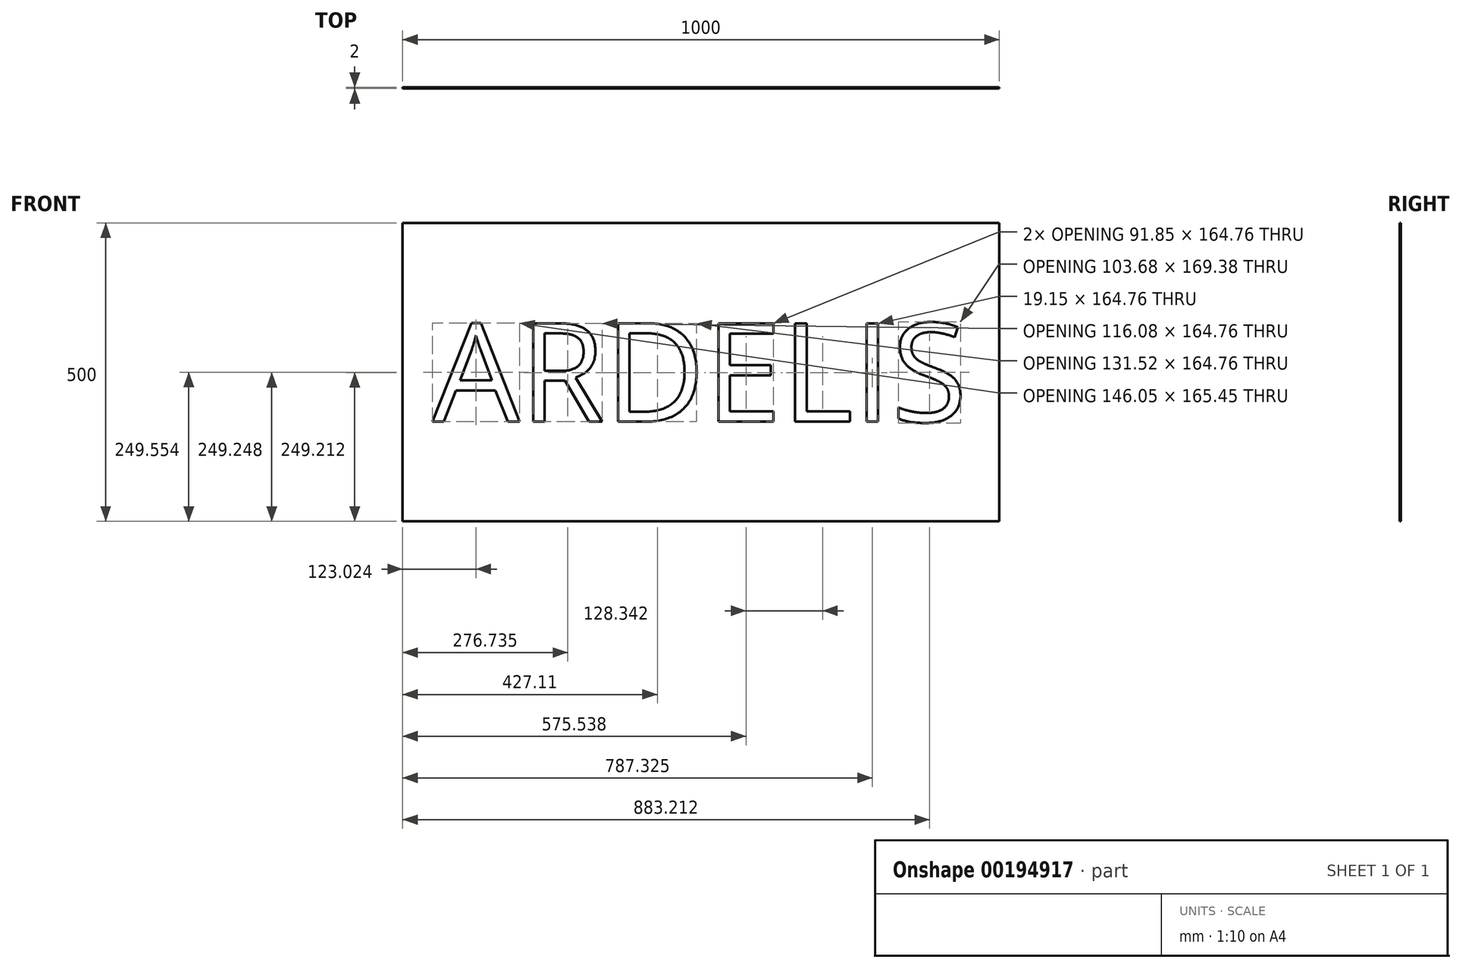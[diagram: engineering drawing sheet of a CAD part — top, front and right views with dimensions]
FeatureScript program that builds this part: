
annotation { "Feature Type Name" : "Feature", "Feature Type Description" : "" }
export const myFeature = defineFeature(function(context is Context, id is Id, definition is map)
    precondition{}
    {
        {
            var Q0;
            Q0=qCreatedBy(makeId("Front.planeOp"),FACE);
            var sketch = newSketch(context, id + "F0", { "sketchPlane" : qUnion([Q0])});
            skLineSegment(sketch, "E0.bottom", {"start": v(500, 250) * mm, "end": v(-500, 250) * mm});
            skLineSegment(sketch, "E0.top", {"start": v(500, -250) * mm, "end": v(-500, -250) * mm});
            skLineSegment(sketch, "E0.left", {"start": v(500, 250) * mm, "end": v(500, -250) * mm});
            skLineSegment(sketch, "E0.right", {"start": v(-500, 250) * mm, "end": v(-500, -250) * mm});
            skPoint(sketch, "E0.middle", {"position": v(0, 0) * mm});
            skSolve(sketch);
        }
        {
            var Q0;
            Q0 = qSketchRegion(id + "F0", true);
            extrude(context, id + "F1", {"entities" : qUnion([Q0]), "depth" : 2 * mm});
        }
        {
            var Q0;
            Q0=makeQuery(id+"F1.opExtrude","CAP_FACE",FACE,{"disambiguationData":[OSD([sQuery(id+"F0.wireOp",EDGE,"E0.bottom"),sQuery(id+"F0.wireOp",EDGE,"E0.top"),sQuery(id+"F0.wireOp",EDGE,"E0.left"),sQuery(id+"F0.wireOp",EDGE,"E0.right")])],"isStart":false});
            var sketch = newSketch(context, id + "F2", { "sketchPlane" : qUnion([Q0])});
            skText(sketch, "E1", { "text": "ARDELIS", "fontName": "OpenSans-Regular.ttf"});
            const initialGuessF2  = {"E1": [-0.45, -0.08317, 1, 0, 0.16617]};
            skSetInitialGuess(sketch, initialGuessF2);
            skSolve(sketch);
        }
        {
            var Q0;
            Q0 = qSketchRegion(id + "F2", true);
            extrude(context, id + "F3", {"entities" : qUnion([Q0]), "operationType" : NewBodyOperationType.REMOVE, "oppositeDirection" : true, "depth" : 2 * mm});
        }
    });
